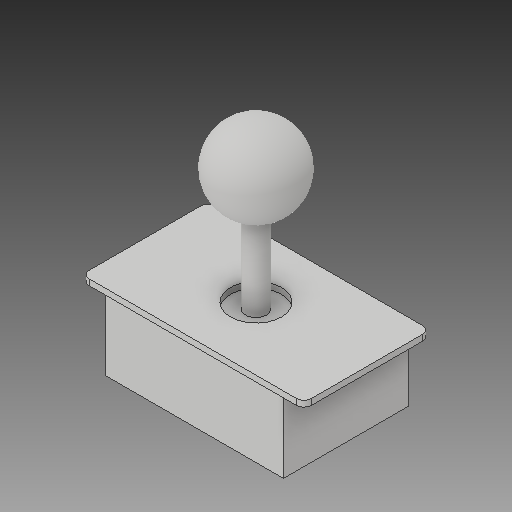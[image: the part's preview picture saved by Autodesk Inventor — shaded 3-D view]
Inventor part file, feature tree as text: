
AUTODESK INVENTOR PART (.ipt)
format: ipt  version: 2017 (Build 210142000, 142)  size: 161,792 bytes
history: native  units: in
note: dims shown in document units (in); Inventor stores cm internally (conversion verified against a paired STEP export)
features: sketch x5, extrude x4, projected_geometry x2, fillet x1, plane x1, revolve x1
ambient origin geometry x8: Origin, YZ Plane, XZ Plane, XY Plane, X Axis, Y Axis, Z Axis, Center Point
bodies: Solid1 (feature_tree)
feature tree (14):
  extrude  "Extrusion1"  Depth=2.126in
  fillet  "Fillet1"  Radius=0.1in
  extrude  "Extrusion2"  Depth=3.0in
  extrude  "Extrusion3"  TaperAngle=0.0deg  [1 undecoded]
  extrude  "Extrusion4"  Depth=1.2in TaperAngle=0.0deg
  plane  "Work Plane1"
  revolve  "Revolution1"  [1 undecoded]
  sketch  "Sketch1"  dims[d0=3.7402in d1=2.126in d2=0.1in d3=0.0in]
  sketch  "Sketch2"  dims[d4=0.125in d5=3.0in]
  projected_geometry  "Projected Loop1"
  sketch  "Sketch3"  dims[d6=2.1in d7=0.0in]
  projected_geometry  "Projected Loop2"
  sketch  "Sketch4"  dims[d8=0.37in d9=1.2in d10=0.0in]
  sketch  "Sketch5"  dims[d11=0.86in d12=0.1in d13=0.0in d14=0.352in d15=1.725in d16=0.0in d17=0.3346in d18=1.378in d19=90.0deg]
note: 2 required parameter values undecoded (feature->parameter linkage not recoverable at this tier; creation-order binding heuristic only, values carry confidence <= 0.55)